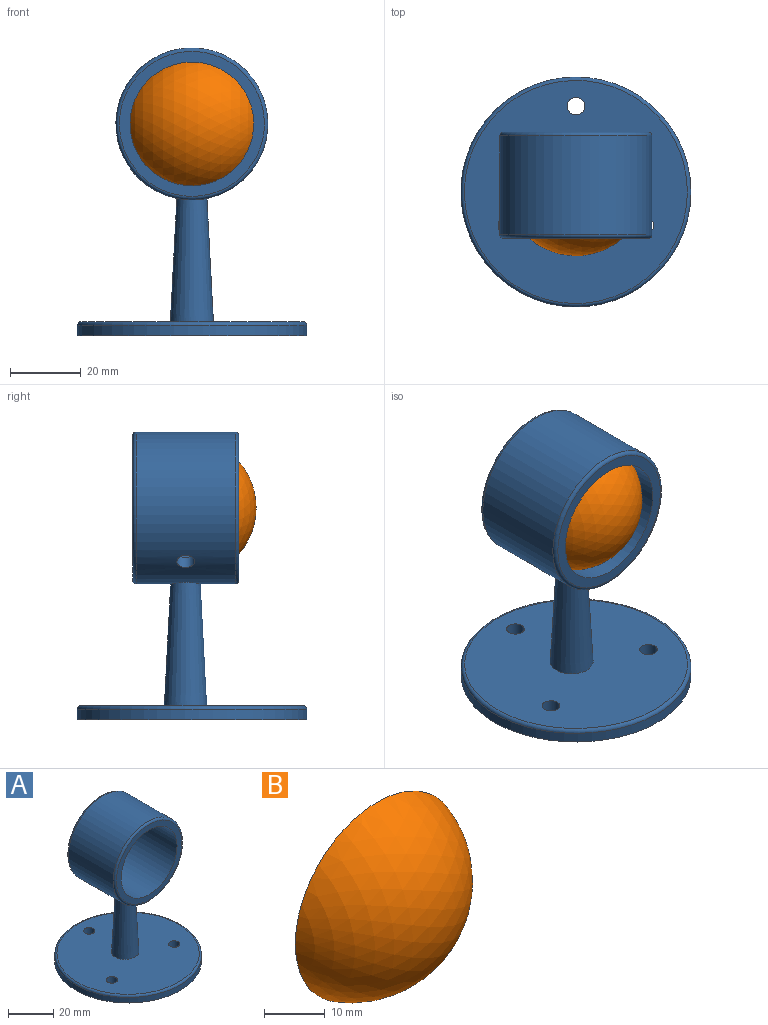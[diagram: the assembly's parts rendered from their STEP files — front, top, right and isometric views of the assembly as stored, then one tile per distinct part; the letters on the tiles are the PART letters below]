
ASSEMBLY  parts=2 mates=1
PART A: 16 faces, bbox 70.4x70.4x83.3 mm
  f0: cylinder r=21.5mm len=43mm, axis (0,1,0), area 3705.5mm2, adj f5,f12,f14,f15
  f1: cylinder r=17.5mm len=35mm, axis (0,1,0), area 2839.2mm2, adj f2,f4,f12
  f2: plane 41x41mm, normal (0,-1,0), area 358.1mm2, adj f1,f15
  f3: plane 41x41mm, normal (0,1,0), area 1320.3mm2, adj f14
  f4: plane 35x35mm, normal (0,-1,0), area 962.1mm2, adj f1
  f5: cone r=6.29mm half-angle=3deg, axis (0,0,-1), area 1129mm2, adj f0,f10
  f6: cylinder r=2.5mm len=5mm, axis (0,0,-1), area 62.8mm2, adj f10,f11
  f7: cylinder r=2.5mm len=5mm, axis (0,0,-1), area 62.8mm2, adj f10,f11
  f8: cylinder r=2.5mm len=5mm, axis (0,0,-1), area 62.8mm2, adj f10,f11
  f9: cylinder r=32.53mm len=65.06mm, axis (0,0,-1), area 613.2mm2, adj f11,f13
  f10: plane 63.06x63.06mm, normal (0,0,1), area 2948.6mm2, adj f5,f6,f7,f8,f13
  f11: plane 65.06x65.06mm, normal (0,0,-1), area 3266mm2, adj f6,f7,f8,f9
  f12: cylinder r=2.5mm len=6.49mm, axis (0.71,0,0.71), area 63.1mm2, adj f0,f1
  f13: torus R=31.53mm, axis (0,0,1), area 317.5mm2, adj f9,f10
  f14: torus R=20.5mm, axis (0,-1,0), area 208.6mm2, adj f0,f3
  f15: torus R=20.5mm, axis (0,-1,0), area 208.6mm2, adj f0,f2
PART B: 3 faces, bbox 38.2x18.3x38.2 mm
  f0: sphere r=20mm, area 1759.1mm2, adj f1
  f1: plane 38.16x38.16mm, normal (0,1,0), area 62mm2, adj f0,f2
  f2: sphere r=19.5mm, area 1653.9mm2, adj f1
PLACE A at identity
PLACE B t=(0,0.03,0)mm
MATE revolute B.f0 <-> A.f0  axis (0,1,0) through (0,0.03,0)mm
